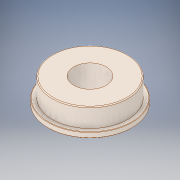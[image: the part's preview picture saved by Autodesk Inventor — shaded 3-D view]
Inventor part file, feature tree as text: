
AUTODESK INVENTOR PART (.ipt)
format: ipt  version: 2018 (Build 220112000, 112)  size: 146,944 bytes
history: native  units: in
note: dims shown in document units (in); Inventor stores cm internally (conversion verified against a paired STEP export)
features: fillet x1
ambient origin geometry x8: Origin, YZ Plane, XZ Plane, XY Plane, X Axis, Y Axis, Z Axis, Center Point
bodies: Solid1 (feature_tree)
feature tree (1):
  fillet  "Fillet2"  [1 undecoded]
note: 1 required parameter value undecoded (feature->parameter linkage not recoverable at this tier; creation-order binding heuristic only, values carry confidence <= 0.55)
